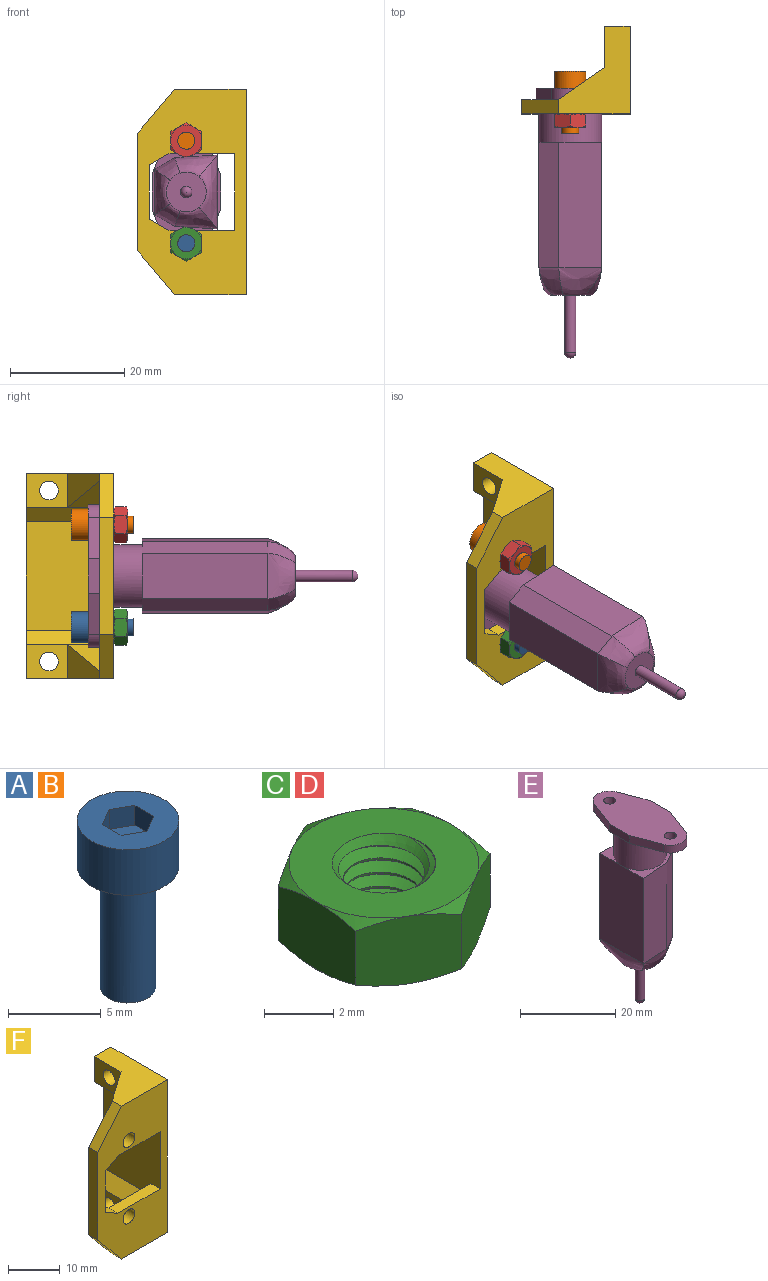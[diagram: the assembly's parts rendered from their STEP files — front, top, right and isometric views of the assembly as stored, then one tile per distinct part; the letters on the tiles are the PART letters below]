
ASSEMBLY  parts=6 mates=6
PART A: 12 faces, bbox 5.5x5.5x11 mm
  f0: plane 5.5x5.5mm, normal (0,0,1), area 18.3mm2, adj f1,f5,f6,f7,f8,f9,f10
  f1: cylinder r=2.75mm len=5.5mm, axis (0,0,-1), area 51.8mm2, adj f0,f2
  f2: plane 5.5x5.5mm, normal (0,0,-1), area 16.7mm2, adj f1,f3
  f3: cylinder r=1.5mm len=8mm, axis (0,0,-1), area 75.4mm2, adj f2,f4
  f4: plane 3x3mm, normal (0,0,-1), area 7.1mm2, adj f3
  f5: plane 1.3x1.25mm, normal (-0.5,-0.87,0), area 1.9mm2, adj f0,f6,f10,f11
  f6: plane 1.44x1.3mm, normal (-1,0,0), area 1.9mm2, adj f0,f5,f7,f11
  f7: plane 1.3x1.25mm, normal (-0.5,0.87,0), area 1.9mm2, adj f0,f6,f8,f11
  f8: plane 1.3x1.25mm, normal (0.5,0.87,0), area 1.9mm2, adj f0,f7,f9,f11
  f9: plane 1.44x1.3mm, normal (1,0,0), area 1.9mm2, adj f0,f8,f10,f11
  f10: plane 1.3x1.25mm, normal (0.5,-0.87,0), area 1.9mm2, adj f0,f5,f9,f11
  f11: plane 2.89x2.5mm, normal (0,0,1), area 5.4mm2, adj f5,f6,f7,f8,f9,f10
PART B: same geometry as A
PART C: 27 faces, bbox 6.6x6.6x3 mm
  f0: cylinder r=1.5mm len=3mm, axis (0,0,-1), area 2.8mm2, adj f10,f11,f12,f13,f14
  f1: cylinder r=1.18mm len=2.35mm, axis (0,0,1), area 1.6mm2, adj f2,f3,f13,f14
  f2: cone r=1.5mm half-angle=45deg, axis (0,0,-1), area 2mm2, adj f1,f11,f13,f14
  f3: cone r=1.5mm half-angle=45deg, axis (0,0,1), area 2mm2, adj f1,f10,f12,f13,f14
  f4: plane 3.01x2.66mm, normal (-0.5,0.87,0), area 7.1mm2, adj f5,f9,f18,f19,f22,f23
  f5: plane 3.44x2.66mm, normal (-1,0,0), area 7.1mm2, adj f4,f6,f17,f18,f23,f24
  f6: plane 3.01x2.66mm, normal (-0.5,-0.87,0), area 7.1mm2, adj f5,f7,f16,f17,f24,f25
  f7: plane 3.01x2.66mm, normal (0.5,-0.87,0), area 7.1mm2, adj f6,f8,f15,f16,f25,f26
  f8: plane 3.44x2.66mm, normal (1,0,0), area 7.1mm2, adj f7,f9,f15,f20,f21,f26
  f9: plane 3.01x2.66mm, normal (0.5,0.87,0), area 7.1mm2, adj f4,f8,f19,f20,f21,f22
  f10: plane 5.5x5.5mm, normal (0,0,1), area 16.7mm2, adj f0,f3,f15,f16,f17,f18,f19,f20
  f11: plane 5.5x5.5mm, normal (0,0,-1), area 16.7mm2, adj f0,f2,f21,f22,f23,f24,f25,f26
  f12: plane 0x0mm, normal (0.5,0.87,0), area 0mm2, adj f0,f3,f13
  f13: bspline ~3x3mm, area 13.2mm2, adj f0,f1,f2,f3,f12
  f14: bspline ~3x3mm, area 13.2mm2, adj f0,f1,f2,f3
  f15: cone r=2.75mm half-angle=60deg, axis (0,0,-1), area 0.7mm2, adj f7,f8,f10
  f16: cone r=2.75mm half-angle=60deg, axis (0,0,-1), area 0.7mm2, adj f6,f7,f10
  f17: cone r=2.75mm half-angle=60deg, axis (0,0,-1), area 0.7mm2, adj f5,f6,f10
  f18: cone r=2.75mm half-angle=60deg, axis (0,0,-1), area 0.7mm2, adj f4,f5,f10
  f19: cone r=2.75mm half-angle=60deg, axis (0,0,-1), area 0.7mm2, adj f4,f9,f10
  f20: cone r=2.75mm half-angle=60deg, axis (0,0,-1), area 0.7mm2, adj f8,f9,f10
  f21: cone r=2.75mm half-angle=60deg, axis (0,0,1), area 0.7mm2, adj f8,f9,f11
  f22: cone r=2.75mm half-angle=60deg, axis (0,0,1), area 0.7mm2, adj f4,f9,f11
  f23: cone r=2.75mm half-angle=60deg, axis (0,0,1), area 0.7mm2, adj f4,f5,f11
  f24: cone r=2.75mm half-angle=60deg, axis (0,0,1), area 0.7mm2, adj f5,f6,f11
  f25: cone r=2.75mm half-angle=60deg, axis (0,0,1), area 0.7mm2, adj f6,f7,f11
  f26: cone r=2.75mm half-angle=60deg, axis (0,0,1), area 0.7mm2, adj f7,f8,f11
PART D: same geometry as C
PART E: 30 faces, bbox 12x25x47.3 mm
  f0: plane 7.01x7.01mm, normal (0,0,-1), area 35.3mm2, adj f22,f23,f24,f25,f26,f27,f28
  f1: plane 11x6.5mm, normal (0,0,1), area 16.9mm2, adj f4,f5,f6,f7,f8
  f2: plane 22x3.5mm, normal (0.5,0.87,0), area 88.7mm2, adj f3,f6,f26,f29
  f3: plane 22x7.5mm, normal (0.07,1,0), area 165.4mm2, adj f2,f7,f27,f29
  f4: plane 22x7.5mm, normal (0.07,-1,0), area 165.4mm2, adj f1,f5,f7,f23
  f5: plane 22x3.5mm, normal (0.5,-0.87,0), area 88.7mm2, adj f1,f4,f6,f24
  f6: plane 22x8mm, normal (1,0,0), area 176mm2, adj f1,f2,f5,f25,f29
  f7: plane 22x13mm, normal (-1,0,0), area 286mm2, adj f1,f3,f4,f28,f29
  f8: cylinder r=5.5mm len=11mm, axis (0,0,-1), area 259.2mm2, adj f1,f9,f29
  f9: plane 25x12mm, normal (0,0,-1), area 122.9mm2, adj f8,f11,f12,f13,f14,f15,f16,f17
  f10: plane 25x12mm, normal (0,0,1), area 218mm2, adj f11,f12,f13,f14,f15,f16,f17,f18
  f11: plane 7.23x2.72mm, normal (-0.94,-0.35,0), area 15.5mm2, adj f9,f10,f12,f18
  f12: cylinder r=3.5mm len=6.55mm, axis (0,0,-1), area 16.9mm2, adj f9,f10,f11,f13
  f13: plane 7.23x2.72mm, normal (0.94,-0.35,0), area 15.5mm2, adj f9,f10,f12,f14
  f14: plane 6x2mm, normal (1,0,0), area 12mm2, adj f9,f10,f13,f15
  f15: plane 7.23x2.72mm, normal (0.94,0.35,0), area 15.5mm2, adj f9,f10,f14,f16
  f16: cylinder r=3.5mm len=6.55mm, axis (0,0,-1), area 16.9mm2, adj f9,f10,f15,f17
  f17: plane 7.23x2.72mm, normal (-0.94,0.35,0), area 15.5mm2, adj f9,f10,f16,f18
  f18: plane 6x2mm, normal (-1,0,0), area 12mm2, adj f9,f10,f11,f17
  f19: cylinder r=1.25mm len=2.5mm, axis (0,0,-1), area 15.7mm2, adj f9,f10
  f20: cylinder r=1.25mm len=2.5mm, axis (0,0,-1), area 15.7mm2, adj f9,f10
  f21: sphere r=1mm, area 6.3mm2, adj f22
  f22: cylinder r=1mm len=10mm, axis (0,0,-1), area 62.8mm2, adj f0,f21
  f23: bspline ~7.5x4.8mm, area 35.4mm2, adj f0,f4,f24,f28
  f24: bspline ~4.8x4.4mm, area 19.5mm2, adj f0,f5,f23,f25
  f25: bspline ~8x4.8mm, area 37.5mm2, adj f0,f6,f24,f26
  f26: bspline ~4.8x4.4mm, area 19.5mm2, adj f0,f2,f25,f27
  f27: bspline ~7.5x4.8mm, area 35.3mm2, adj f0,f3,f26,f28
  f28: bspline ~13x4.8mm, area 58.9mm2, adj f0,f7,f23,f27
  f29: plane 11x6.5mm, normal (0,0,1), area 16.9mm2, adj f2,f3,f6,f7,f8
PART F: 27 faces, bbox 19x15.4x36 mm
  f0: plane 7.25x6mm, normal (-1,0,0), area 34.9mm2, adj f6,f8,f10,f22,f26
  f1: plane 36x17mm, normal (0,1,0), area 255.6mm2, adj f4,f5,f6,f11,f12,f13,f14,f15
  f2: plane 36x15.4mm, normal (1,0,0), area 537.3mm2, adj f7,f8,f9,f10,f21,f22
  f3: plane 7.25x6mm, normal (-1,0,0), area 34.9mm2, adj f4,f7,f10,f21,f24
  f4: plane 12.9x2.5mm, normal (-0.71,0,0.71), area 45.6mm2, adj f1,f3,f5,f10,f23
  f5: plane 19x15.4mm, normal (-1,0,0), area 278.9mm2, adj f1,f4,f6,f9,f10,f14,f18
  f6: plane 12.9x2.5mm, normal (-0.71,0,-0.71), area 45.6mm2, adj f0,f1,f5,f10,f25
  f7: plane 15.4x12.57mm, normal (0,0,-1), area 112.3mm2, adj f2,f3,f9,f10,f13,f24
  f8: plane 15.4x12.57mm, normal (0,0,1), area 112.3mm2, adj f0,f2,f9,f10,f11,f26
  f9: plane 36x19mm, normal (0,-1,0), area 423.1mm2, adj f2,f5,f7,f8,f11,f12,f13,f14
  f10: plane 36x4.5mm, normal (0,1,0), area 108.2mm2, adj f0,f2,f3,f4,f5,f6,f7,f8
  f11: plane 7.66x6.43mm, normal (-0.77,0,0.64), area 25mm2, adj f1,f8,f9,f12
  f12: plane 20.68x2.5mm, normal (-1,0,0), area 51.7mm2, adj f1,f9,f11,f13
  f13: plane 7.66x6.43mm, normal (-0.77,0,-0.64), area 25mm2, adj f1,f7,f9,f12
  f14: plane 11.54x2.5mm, normal (0,0,1), area 28.8mm2, adj f1,f5,f9,f15
  f15: plane 3.46x2.5mm, normal (0.5,0,0.87), area 10mm2, adj f1,f9,f14,f16
  f16: plane 9.5x2.5mm, normal (1,0,0), area 23.8mm2, adj f1,f9,f15,f17
  f17: plane 3.46x2.5mm, normal (0.5,0,-0.87), area 10mm2, adj f1,f9,f16,f18
  f18: plane 11.54x2.5mm, normal (0,0,-1), area 28.8mm2, adj f1,f5,f9,f17
  f19: cylinder r=1.6mm len=3.2mm, axis (0,-1,0), area 25.1mm2, adj f1,f9
  f20: cylinder r=1.6mm len=3.2mm, axis (0,-1,0), area 25.1mm2, adj f1,f9
  f21: cylinder r=1.65mm len=4.5mm, axis (1,0,0), area 46.7mm2, adj f2,f3
  f22: cylinder r=1.65mm len=4.5mm, axis (1,0,0), area 46.7mm2, adj f0,f2
  f23: plane 8.07x5.65mm, normal (-0.5,0,0.87), area 26.3mm2, adj f1,f4,f24
  f24: plane 8.07x6mm, normal (-0.57,0.82,0), area 36.2mm2, adj f1,f3,f7,f23
  f25: plane 8.07x5.65mm, normal (-0.5,0,-0.87), area 26.3mm2, adj f1,f6,f26
  f26: plane 8.07x6mm, normal (-0.57,0.82,0), area 36.2mm2, adj f0,f1,f8,f25
PLACE A rot(axis=(-1,0,0),90deg) t=(-50.41,-11.72,10.6)mm
PLACE B rot(axis=(-1,0,0),90deg) t=(-50.41,-11.72,28.6)mm
PLACE C rot(axis=(0,0.71,-0.71),180deg) t=(-30.41,-17.42,10.6)mm
PLACE D rot(axis=(0,0.71,-0.71),180deg) t=(-30.41,-17.42,28.6)mm
PLACE E rot(axis=(0,0.71,0.71),180deg) t=(-4.42,-53.32,8.62)mm
PLACE F t=(2.25,1.4,0)mm
MATE fastened C.f0 <-> F.f20  axis (0,1,0) through (-30.41,-16.22,10.6)mm
MATE fastened D.f0 <-> F.f19  axis (0,1,0) through (-30.41,-16.22,28.6)mm
MATE fastened A.f1 <-> E.f12  axis (0,-1,0) through (-30.41,-11.72,10.6)mm
MATE fastened E.f16 <-> F.f19  axis (0,-1,0) through (-30.41,-13.72,28.6)mm
MATE fastened E.f12 <-> F.f20  axis (0,-1,0) through (-30.41,-13.72,10.6)mm
MATE fastened B.f1 <-> E.f16  axis (0,-1,0) through (-30.41,-11.72,28.6)mm
